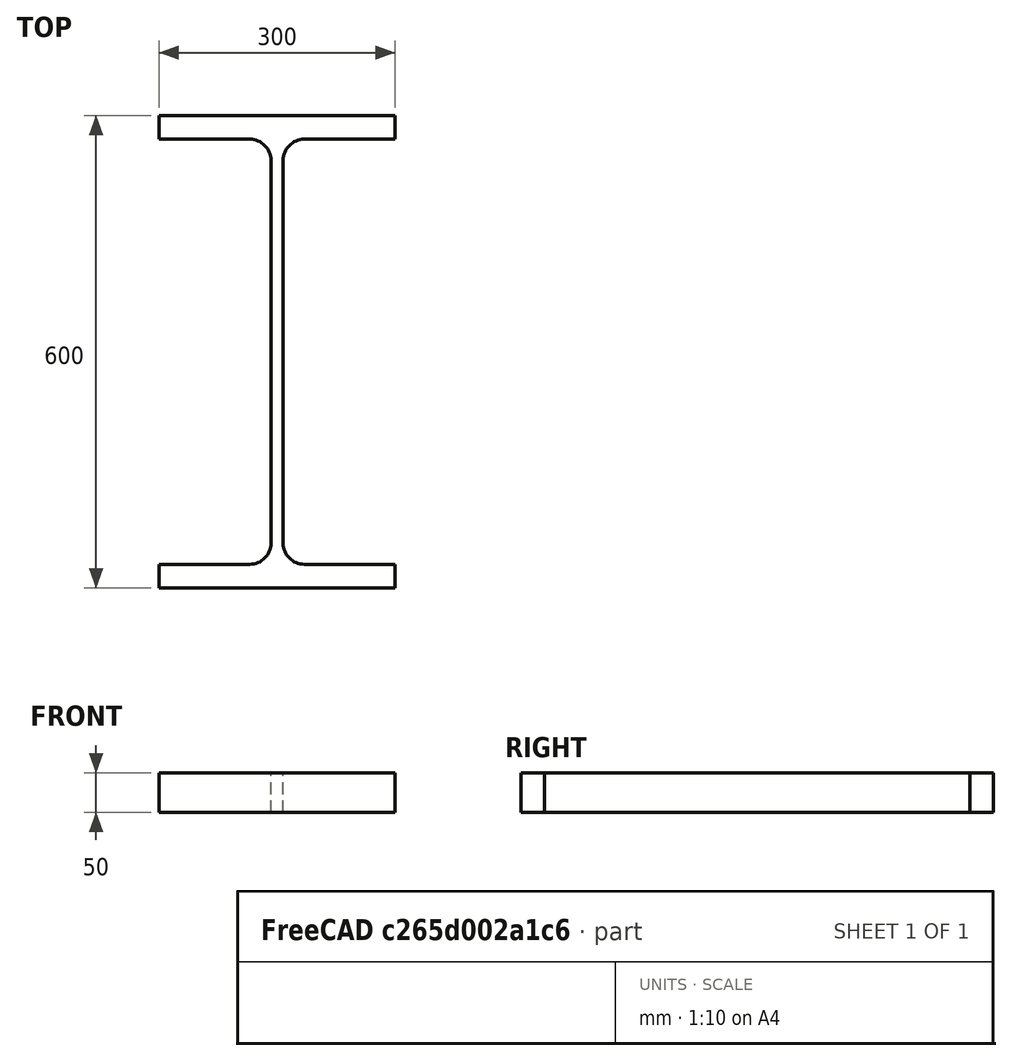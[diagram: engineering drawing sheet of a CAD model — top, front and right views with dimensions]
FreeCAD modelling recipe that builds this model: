
FCSTD DOCUMENT  (FreeCAD 0.15R4671 (Git))
Label: HE-B-Profile 600 DIN1025-2 S235JR
License: All rights reserved
LicenseURL: http://en.wikipedia.org/wiki/All_rights_reserved
objects: Sketcher::SketchObject×1, Part::Extrusion×1
note: 2 computed .brp shape members not serialized (recipe doc carries the construction recipe); baked Part::Feature solids carry a one-line shape summary decoded from their .brp

FEATURE [Sketcher::SketchObject] Sketch
  sketch-geometry (16):
    g0: LineSegment StartX=7.75 StartY=-243 StartZ=0 EndX=7.75 EndY=243 EndZ=0
    g1: LineSegment StartX=34.75 StartY=270 StartZ=0 EndX=150 EndY=270 EndZ=0
    g2: LineSegment StartX=150 StartY=270 StartZ=0 EndX=150 EndY=300 EndZ=0
    g3: LineSegment StartX=150 StartY=300 StartZ=0 EndX=-150 EndY=300 EndZ=0
    g4: LineSegment StartX=-150 StartY=300 StartZ=0 EndX=-150 EndY=270 EndZ=0
    g5: LineSegment StartX=-150 StartY=270 StartZ=0 EndX=-34.75 EndY=270 EndZ=0
    g6: LineSegment StartX=-7.75 StartY=243 StartZ=0 EndX=-7.75 EndY=-243 EndZ=0
    g7: LineSegment StartX=-34.75 StartY=-270 StartZ=0 EndX=-150 EndY=-270 EndZ=0
    g8: LineSegment StartX=-150 StartY=-270 StartZ=0 EndX=-150 EndY=-300 EndZ=0
    g9: LineSegment StartX=-150 StartY=-300 StartZ=0 EndX=150 EndY=-300 EndZ=0
    g10: LineSegment StartX=150 StartY=-300 StartZ=0 EndX=150 EndY=-270 EndZ=0
    g11: LineSegment StartX=150 StartY=-270 StartZ=0 EndX=34.75 EndY=-270 EndZ=0
    g12: ArcOfCircle CenterX=34.75 CenterY=243 CenterZ=0 NormalX=0 NormalY=0 NormalZ=1 Radius=27 StartAngle=1.5708 EndAngle=3.14159
    g13: ArcOfCircle CenterX=34.75 CenterY=-243 CenterZ=0 NormalX=0 NormalY=0 NormalZ=1 Radius=27 StartAngle=3.14159 EndAngle=4.71239
    g14: ArcOfCircle CenterX=-34.75 CenterY=243 CenterZ=0 NormalX=0 NormalY=0 NormalZ=1 Radius=27 StartAngle=0 EndAngle=1.5708
    g15: ArcOfCircle CenterX=-34.75 CenterY=-243 CenterZ=0 NormalX=0 NormalY=0 NormalZ=1 Radius=27 StartAngle=4.71239 EndAngle=6.28319
  constraints (42):
    c: Vertical(g0)
    c: Coincident(g2,g1)
    c: Vertical(g2)
    c: Coincident(g3,g2)
    c: Coincident(g4,g3)
    c: Vertical(g4)
    c: Coincident(g5,g4)
    c: Horizontal(g5)
    c: Vertical(g6)
    c: Horizontal(g7)
    c: Coincident(g8,g7)
    c: Vertical(g8)
    c: Coincident(g9,g8)
    c: Horizontal(g9)
    c: Coincident(g10,g9)
    c: Vertical(g10)
    c: Coincident(g11,g10)
    c: Horizontal(g11)
    c: Tangent(g1,g12) = 1.5708
    c: Tangent(g0,g12) = 1.5708
    c: Tangent(g0,g13) = 1.5708
    c: Tangent(g11,g13) = 1.5708
    c: Tangent(g5,g14) = 1.5708
    c: Tangent(g6,g14) = 1.5708
    c: Tangent(g6,g15) = 1.5708
    c: Tangent(g7,g15) = 1.5708
    c: Equal(g3,g9)
    c: Equal(g2,g4)
    c: Equal(g4,g8)
    c: Equal(g8,g10)
    c: Equal(g12,g14)
    c: Equal(g14,g15)
    c: Equal(g15,g13)
    c: Symmetric(g2,g3,g-2)
    c: Symmetric(g9,g8,g-2)
    c: Symmetric(g0,g6,g-2)
    c: Symmetric(g2,g9,g-1)
    c: DistanceY(g2,g9) = -600
    c: DistanceX(g3) = -300
    c: DistanceX(g0,g6) = -15.5
    c: DistanceY(g2) = 30
    c: Radius(g12) = 27
FEATURE [Part::Extrusion] Extrude  label="HE-B-Profile 600 DIN1025-2 S235JR"
  Base = -> Sketch
  Dir = (0,0,50)
  Solid = true
